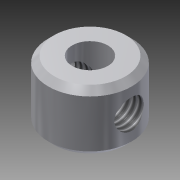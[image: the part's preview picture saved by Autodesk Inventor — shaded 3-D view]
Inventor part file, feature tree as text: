
AUTODESK INVENTOR PART (.ipt)
format: ipt  version: 2015 (Build 190159000, 159)  size: 154,112 bytes
history: native  units: mm
features: sketch x4, extrude x2, hole x2, other x1, chamfer x1
ambient origin geometry x8: Origin, YZ Plane, XZ Plane, XY Plane, X Axis, Y Axis, Z Axis, Center Point
bodies: Body1 (feature_tree)
feature tree (10):
  other  "ソリッド1"
  extrude  "押し出し1"  Depth=7.0mm
  hole  "穴1"  [1 undecoded]
  extrude  "押し出し2"  Depth=5.0mm TaperAngle=0.0deg
  hole  "穴2"  [1 undecoded]
  chamfer  "面取り1"  Distance=3.5mm
  sketch  "スケッチ1"
  sketch  "スケッチ2"
  sketch  "スケッチ3"
  sketch  "スケッチ4"
note: 2 required parameter values undecoded (feature->parameter linkage not recoverable at this tier; creation-order binding heuristic only, values carry confidence <= 0.55)
